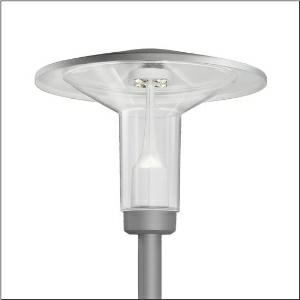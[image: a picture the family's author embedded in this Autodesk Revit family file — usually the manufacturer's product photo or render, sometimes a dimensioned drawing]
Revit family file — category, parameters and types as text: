
# Revit family: laterne_iq___p1_0a_5xa5255bf14h_d88c
name_source: partatom
category: Lighting Fixtures
units: mm (PartAtom-declared; Revit-internal decimal feet)

## family parameters
Cut with Voids When Loaded = No
Host = Face
Light Source = No
Part Type = Normal
Room Calculation Point = No
Round Connector Dimension = Use Diameter
Shared = No

## types (1)
- --- (1 x LED, 1510 lm, 12.9 W, 2200K)
    Apparent Load = 13 VA
    CIE Flux Codes = 35 64 91 96 100
    Color Rendering = 70
    Color Temperature = 2200K
    Default Elevation = 1800 mm
    Description = Lantern iQ, mast luminaire, Module 540 iQ-SR, primary light control with 3 zone facetted reflector, of plastic, silver coated, highly specular, structured, primary optical cover: cover, of PMMA, transparent, light distribution: P1.0a, light emission: direct distribution, primary light characteristic: strongly asymmetric, installation type: post-top, LED, High Power LED, rated luminous flux: 1.510lm, luminous efficacy: 117lm/W, light colour: 722, colour temperature: 2200K, control gear: iQ Street-Remote, control: pre-setting: logarithmic dimming characteristic, Street-Remote, Auto-Match, Temp-Guard, Lumen-Switch, Night-Set, Smart-Wire, Light-Fading, Desk-Remote (wireless, voltage-free reading and setting of iQ features in the workshop via application-optimized NFC function/RFID function), optimised constant luminous flux control (CLO 2.0), with terminal, 6-pole, max. 2.5mm², mains connection: 230..240V, AC, 50/60Hz, start of lifetime: 13W, end of service life: 13W, reduction: 6W, luminaire housing, upper part, of glass-fibre reinforced polyester, coated, Siteco® metallic grey (DB 702S), diameter: 750mm, height: 583mm, spigot size: d x l = 76 x 70mm (post-top) | with reducer (optional accessory) 60 x 70mm, mounting height: 3..5m, post-top mast mounting element, of diecast aluminium, coated, Siteco® metallic grey (DB 702S), Module 540 iQ-SR, traffic white (RAL 9016), equipment: standard, protection rating (complete): IP65, insulation class (complete): insulation class II (safety insulation), certification: CE, ENEC, VDE, packaging unit: 1 piece

Light Distribution: P1.0a
    Height = 583 mm
    Lamp = 1 x LED
    Lamp Light Flux = 1510 lm
    Lamp Power = 12.9 W
    Lamp count = 1
    Length = 750 mm
    Luminous efficacy = 117 lm/W
    Manufacturer = Siteco
    ModVariant = No
    Model = 5XA5255BF14H
    Number of Poles = 1
    OnlyDefault = Yes
    Power Factor = 1
    Product Name = Laterne iQ | P1.0a
    Product group = mast luminaire | pylon top
    ProductGroupID = 6100
    Protection Class = Protection class II
    Protection Degree = IP 65
    RLX_Detail_Level = 1
    RLX_Emergency_Light_Flux = 0 lm
    RLX_Emergency_Type = 0
    RLX_Emergency_Type_DB = No
    RlxData = <blob elided: 59421 chars, md5=bfdf2036>
    Socket = socket
    Standby Power = 0 W
    System Light Flux = 1510 lm
    System Power = 13 W
    Type Comments = factory setting: luminous flux: 100 % | dim-lin: 254 | 516 mA
    Type Image = l_1006050.jpg
    URL = http://relux.com
    VarID = @adj_160562
    Voltage = 0 V
    Weight = 0.00 kg
    Width = 0 mm  [stored 0 ft]

note: [stored X ft] marks values corroborated as IEEE doubles in the binary element streams (Revit-internal decimal feet)

## geometry (parser evidence)
native form markers: Blend x4, Sweep x10
no freeform markers — native parametric forms only
